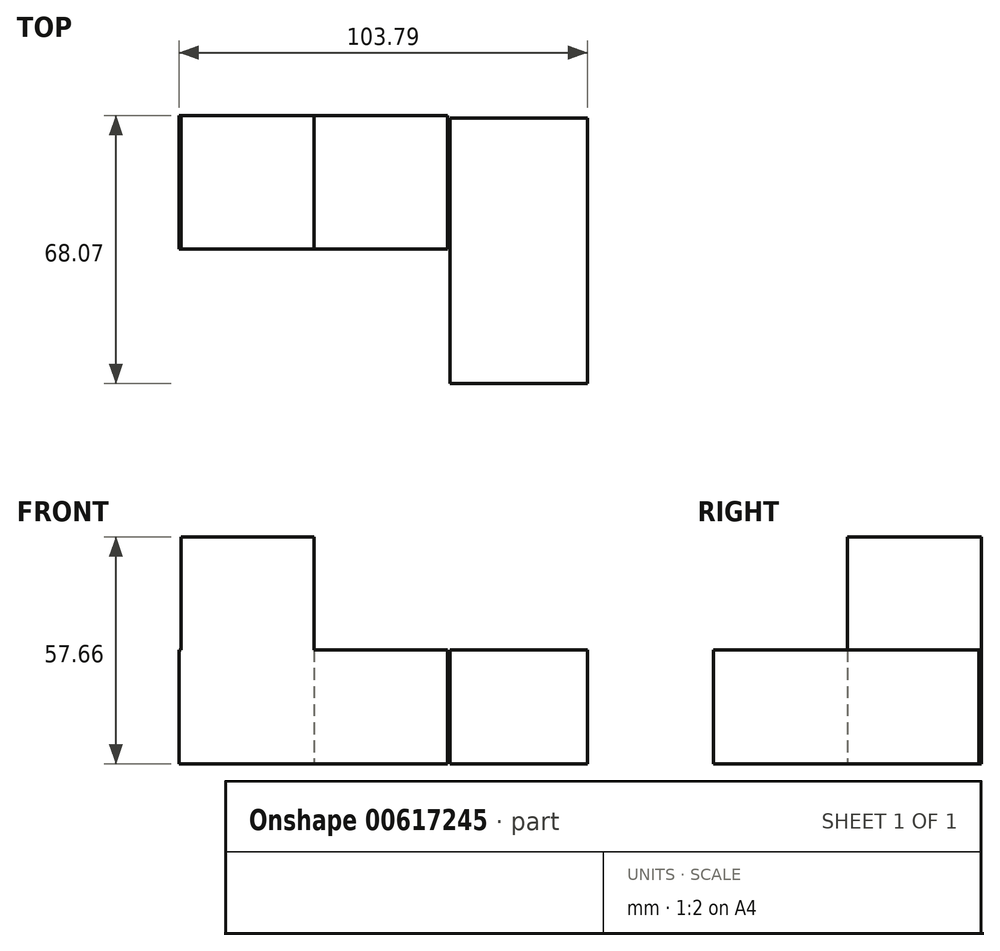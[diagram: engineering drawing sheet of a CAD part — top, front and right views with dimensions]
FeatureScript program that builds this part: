
annotation { "Feature Type Name" : "Feature", "Feature Type Description" : "" }
export const myFeature = defineFeature(function(context is Context, id is Id, definition is map)
    precondition{}
    {
        {
            var Q0;
            Q0=qCreatedBy(makeId("Top.planeOp"),FACE);
            var sketch = newSketch(context, id + "F0", { "sketchPlane" : qUnion([Q0])});
            skLineSegment(sketch, "E0.bottom", {"start": v(-90.16, 53.71) * mm, "end": v(-41.48, 53.71) * mm});
            skLineSegment(sketch, "E0.top", {"start": v(-90.16, 0) * mm, "end": v(-41.48, 0) * mm});
            skLineSegment(sketch, "E0.left", {"start": v(-90.16, 53.71) * mm, "end": v(-90.16, 0) * mm});
            skLineSegment(sketch, "E0.right", {"start": v(-41.48, 53.71) * mm, "end": v(-41.48, 0) * mm});
            skLineSegment(sketch, "E1.bottom", {"start": v(-41.48, 53.71) * mm, "end": v(13.17, 53.71) * mm});
            skLineSegment(sketch, "E1.top", {"start": v(-41.48, 0) * mm, "end": v(13.17, 0) * mm});
            skLineSegment(sketch, "E1.right", {"start": v(13.17, 53.71) * mm, "end": v(13.17, 0) * mm});
            skLineSegment(sketch, "E2.bottom", {"start": v(13.17, 53.71) * mm, "end": v(65.3, 53.71) * mm});
            skLineSegment(sketch, "E2.top", {"start": v(13.17, 0) * mm, "end": v(65.3, 0) * mm});
            skLineSegment(sketch, "E2.right", {"start": v(65.3, 53.71) * mm, "end": v(65.3, 0) * mm});
            skLineSegment(sketch, "E3.bottom", {"start": v(65.3, 0) * mm, "end": v(13.17, 0) * mm});
            skLineSegment(sketch, "E3.top", {"start": v(65.3, -53.49) * mm, "end": v(13.17, -53.49) * mm});
            skLineSegment(sketch, "E3.left", {"start": v(65.3, 0) * mm, "end": v(65.3, -53.49) * mm});
            skLineSegment(sketch, "E3.right", {"start": v(13.17, 0) * mm, "end": v(13.17, -53.49) * mm});
            skSolve(sketch);
        }
        {
            var Q0;
            Q0 = qSketchRegion(id + "F0", true);
            extrude(context, id + "F1", {"entities" : qUnion([Q0]), "depth" : 34.04 * mm, "offsetDistance" : 25.4 * mm});
        }
        {
            var Q0;
            Q0=makeQuery(id+"F1.opExtrude","CAP_FACE",FACE,{"disambiguationData":[OSD([sQuery(id+"F0.wireOp",EDGE,"E0.bottom"),sQuery(id+"F0.wireOp",EDGE,"E0.top"),sQuery(id+"F0.wireOp",EDGE,"E0.left"),sQuery(id+"F0.wireOp",EDGE,"E1.bottom"),sQuery(id+"F0.wireOp",EDGE,"E1.top"),sQuery(id+"F0.wireOp",EDGE,"E2.bottom"),sQuery(id+"F0.wireOp",EDGE,"E2.right"),sQuery(id+"F0.wireOp",EDGE,"E3.top"),sQuery(id+"F0.wireOp",EDGE,"E3.left"),sQuery(id+"F0.wireOp",EDGE,"E3.right")])],"isStart":false});
            var sketch = newSketch(context, id + "F2", { "sketchPlane" : qUnion([Q0])});
            skLineSegment(sketch, "E4.bottom", {"start": v(-90.16, 53.71) * mm, "end": v(-36.28, 53.71) * mm});
            skLineSegment(sketch, "E4.top", {"start": v(-90.16, 0) * mm, "end": v(-36.28, 0) * mm});
            skLineSegment(sketch, "E4.left", {"start": v(-90.16, 53.71) * mm, "end": v(-90.16, 0) * mm});
            skLineSegment(sketch, "E4.right", {"start": v(-36.28, 53.71) * mm, "end": v(-36.28, 0) * mm});
            skSolve(sketch);
        }
        {
            var Q0;
            Q0 = qSketchRegion(id + "F2", true);
            extrude(context, id + "F3", {"entities" : qUnion([Q0]), "operationType" : NewBodyOperationType.ADD, "depth" : 37.34 * mm, "offsetDistance" : 25.4 * mm});
        }
        {
            var Q0;
            Q0=makeQuery(id+"F1.opExtrude","SWEPT_BODY",BODY,{"disambiguationData":[OSD([sQuery(id+"F0.wireOp",EDGE,"E0.bottom"),sQuery(id+"F0.wireOp",EDGE,"E0.top"),sQuery(id+"F0.wireOp",EDGE,"E0.left"),sQuery(id+"F0.wireOp",EDGE,"E1.bottom"),sQuery(id+"F0.wireOp",EDGE,"E1.top"),sQuery(id+"F0.wireOp",EDGE,"E2.bottom"),sQuery(id+"F0.wireOp",EDGE,"E2.right"),sQuery(id+"F0.wireOp",EDGE,"E3.top"),sQuery(id+"F0.wireOp",EDGE,"E3.left"),sQuery(id+"F0.wireOp",EDGE,"E3.right")])]});
            deleteBodies(context, id + "F4", {"entities" : qUnion([Q0])});
        }
        {
            var Q0;
            Q0=qCreatedBy(makeId("Top.planeOp"),FACE);
            var sketch = newSketch(context, id + "F5", { "sketchPlane" : qUnion([Q0])});
            skLineSegment(sketch, "E5.bottom", {"start": v(0, 0) * mm, "end": v(-34.31, 0) * mm});
            skLineSegment(sketch, "E5.top", {"start": v(0, 33.96) * mm, "end": v(-34.31, 33.96) * mm});
            skLineSegment(sketch, "E5.left", {"start": v(0, 0) * mm, "end": v(0, 33.96) * mm});
            skLineSegment(sketch, "E5.right", {"start": v(-34.31, 0) * mm, "end": v(-34.31, 33.96) * mm});
            skLineSegment(sketch, "E6.bottom", {"start": v(0, 0) * mm, "end": v(33.96, 0) * mm});
            skLineSegment(sketch, "E6.top", {"start": v(0, 33.96) * mm, "end": v(33.96, 33.96) * mm});
            skLineSegment(sketch, "E6.right", {"start": v(33.96, 0) * mm, "end": v(33.96, 33.96) * mm});
            skSolve(sketch);
        }
        {
            var Q0;
            Q0=qCreatedBy(makeId("Top.planeOp"),FACE);
            var sketch = newSketch(context, id + "F6", { "sketchPlane" : qUnion([Q0])});
            skLineSegment(sketch, "E7.bottom", {"start": v(34.57, 33.35) * mm, "end": v(69.48, 33.35) * mm});
            skLineSegment(sketch, "E7.top", {"start": v(34.57, 0) * mm, "end": v(69.48, 0) * mm});
            skLineSegment(sketch, "E7.left", {"start": v(34.57, 33.35) * mm, "end": v(34.57, 0) * mm});
            skLineSegment(sketch, "E7.right", {"start": v(69.48, 33.35) * mm, "end": v(69.48, 0) * mm});
            skLineSegment(sketch, "E8.top", {"start": v(34.57, -34.11) * mm, "end": v(69.48, -34.11) * mm});
            skLineSegment(sketch, "E8.left", {"start": v(34.57, 0) * mm, "end": v(34.57, -34.11) * mm});
            skLineSegment(sketch, "E8.right", {"start": v(69.48, 0) * mm, "end": v(69.48, -34.11) * mm});
            skSolve(sketch);
        }
        {
            var Q0;
            Q0 = qSketchRegion(id + "F6", true);
            var Q1;
            {var subQ0=sQuery(id+"F5.wireOp",EDGE,"E5.bottom");Q1=makeQuery(id+"F5.imprint","IMPRINT",FACE,{"disambiguationData":[TD([[makeQuery(id+"F5.imprint","IMPRINT",EDGE,{"derivedFrom":subQ0}),-1.0]])]});}
            var Q2;
            {var subQ3=sQuery(id+"F5.wireOp",EDGE,"E6.bottom");Q2=makeQuery(id+"F5.imprint","IMPRINT",FACE,{"disambiguationData":[TD([[makeQuery(id+"F5.imprint","IMPRINT",EDGE,{"derivedFrom":subQ3}),1.0]])]});}
            extrude(context, id + "F7", {"entities" : qUnion([Q0, Q1, Q2]), "depth" : 28.96 * mm, "offsetDistance" : 25.4 * mm});
        }
        {
            var Q0;
            Q0=makeQuery(id+"F7.opExtrude","CAP_FACE",FACE,{"disambiguationData":[OSD([sQuery(id+"F5.wireOp",EDGE,"E5.bottom"),sQuery(id+"F5.wireOp",EDGE,"E5.top"),sQuery(id+"F5.wireOp",EDGE,"E5.right"),sQuery(id+"F5.wireOp",EDGE,"E6.bottom"),sQuery(id+"F5.wireOp",EDGE,"E6.top"),sQuery(id+"F5.wireOp",EDGE,"E5.left"),sQuery(id+"F5.wireOp",EDGE,"E6.right")])],"isStart":false});
            var sketch = newSketch(context, id + "F8", { "sketchPlane" : qUnion([Q0])});
            skSolve(sketch);
        }
        {
            var Q0;
            Q0=makeQuery(id+"F8.imprint","IMPRINT",FACE,{"disambiguationData":[TD([[makeQuery(id+"F8.imprint","IMPRINT",EDGE,{"derivedFrom":makeQuery(id+"F7.opExtrude","CAP_EDGE",EDGE,{"disambiguationData":[OSD([sQuery(id+"F5.wireOp",EDGE,"E5.top")])],"isStart":false})}),1.0]])]});
            var sketch = newSketch(context, id + "F9", { "sketchPlane" : qUnion([Q0])});
            skLineSegment(sketch, "E9.bottom", {"start": v(0, 0) * mm, "end": v(-33.8, 0) * mm});
            skLineSegment(sketch, "E9.top", {"start": v(0, 35.1) * mm, "end": v(-33.8, 35.1) * mm});
            skLineSegment(sketch, "E9.left", {"start": v(0, 0) * mm, "end": v(0, 35.1) * mm});
            skLineSegment(sketch, "E9.right", {"start": v(-33.8, 0) * mm, "end": v(-33.8, 35.1) * mm});
            skSolve(sketch);
        }
        {
            var Q0;
            {var subQ0=sQuery(id+"F9.wireOp",EDGE,"E9.bottom");Q0=makeQuery(id+"F9.imprint","IMPRINT",FACE,{"disambiguationData":[TD([[makeQuery(id+"F9.imprint","IMPRINT",EDGE,{"derivedFrom":subQ0}),-1.0]])]});}
            extrude(context, id + "F10", {"entities" : qUnion([Q0]), "operationType" : NewBodyOperationType.ADD, "depth" : 28.7 * mm, "offsetDistance" : 25.4 * mm});
        }
    });
